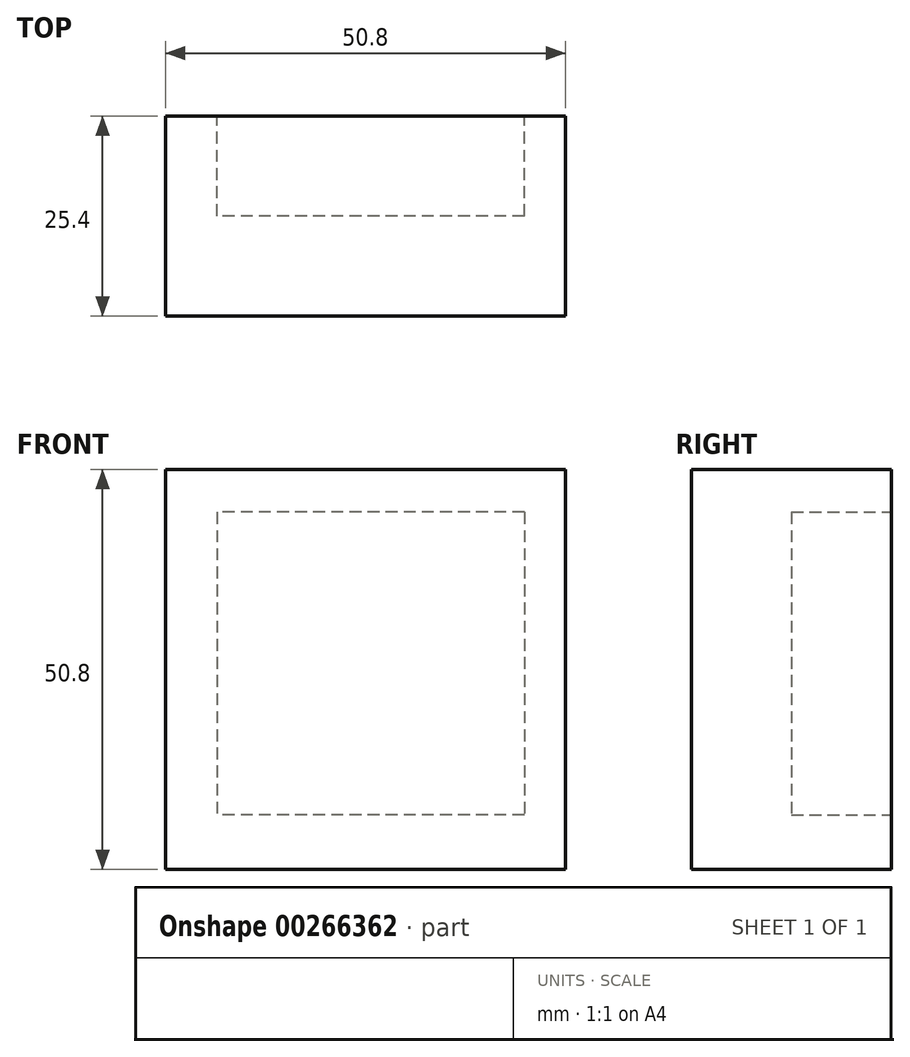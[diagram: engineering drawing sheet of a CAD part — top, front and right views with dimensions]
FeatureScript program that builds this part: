
annotation { "Feature Type Name" : "Feature", "Feature Type Description" : "" }
export const myFeature = defineFeature(function(context is Context, id is Id, definition is map)
    precondition{}
    {
        {
            var Q0;
            Q0=qCreatedBy(makeId("Front.planeOp"),FACE);
            var sketch = newSketch(context, id + "F0", { "sketchPlane" : qUnion([Q0])});
            skLineSegment(sketch, "E0.bottom", {"start": v(-10.24, 18.86) * mm, "end": v(-61.04, 18.86) * mm});
            skLineSegment(sketch, "E0.top", {"start": v(-10.24, -31.94) * mm, "end": v(-61.04, -31.94) * mm});
            skLineSegment(sketch, "E0.left", {"start": v(-10.24, 18.86) * mm, "end": v(-10.24, -31.94) * mm});
            skLineSegment(sketch, "E0.right", {"start": v(-61.04, 18.86) * mm, "end": v(-61.04, -31.94) * mm});
            skSolve(sketch);
        }
        {
            var Q0;
            Q0 = qSketchRegion(id + "F0", true);
            extrude(context, id + "F1", {"entities" : qUnion([Q0]), "depth" : 25.4 * mm});
        }
        {
            var Q0;
            Q0=makeQuery(id+"F1.opExtrude","CAP_FACE",FACE,{"disambiguationData":[OSD([sQuery(id+"F0.wireOp",EDGE,"E0.bottom"),sQuery(id+"F0.wireOp",EDGE,"E0.top"),sQuery(id+"F0.wireOp",EDGE,"E0.left"),sQuery(id+"F0.wireOp",EDGE,"E0.right")])],"isStart":true});
            var sketch = newSketch(context, id + "F2", { "sketchPlane" : qUnion([Q0])});
            skLineSegment(sketch, "E1.bottom", {"start": v(15.48, 13.45) * mm, "end": v(54.52, 13.45) * mm});
            skLineSegment(sketch, "E1.top", {"start": v(15.48, -24.98) * mm, "end": v(54.52, -24.98) * mm});
            skLineSegment(sketch, "E1.left", {"start": v(15.48, 13.45) * mm, "end": v(15.48, -24.98) * mm});
            skLineSegment(sketch, "E1.right", {"start": v(54.52, 13.45) * mm, "end": v(54.52, -24.98) * mm});
            skSolve(sketch);
        }
        {
            var Q0;
            Q0=makeQuery(id+"F2.imprint","IMPRINT",FACE,{"disambiguationData":[TD([[makeQuery(id+"F2.imprint","IMPRINT",EDGE,{"derivedFrom":sQuery(id+"F2.wireOp",EDGE,"E1.bottom")}),-1.0]])]});
            extrude(context, id + "F3", {"entities" : qUnion([Q0]), "operationType" : NewBodyOperationType.REMOVE, "oppositeDirection" : true, "depth" : 12.7 * mm});
        }
    });
